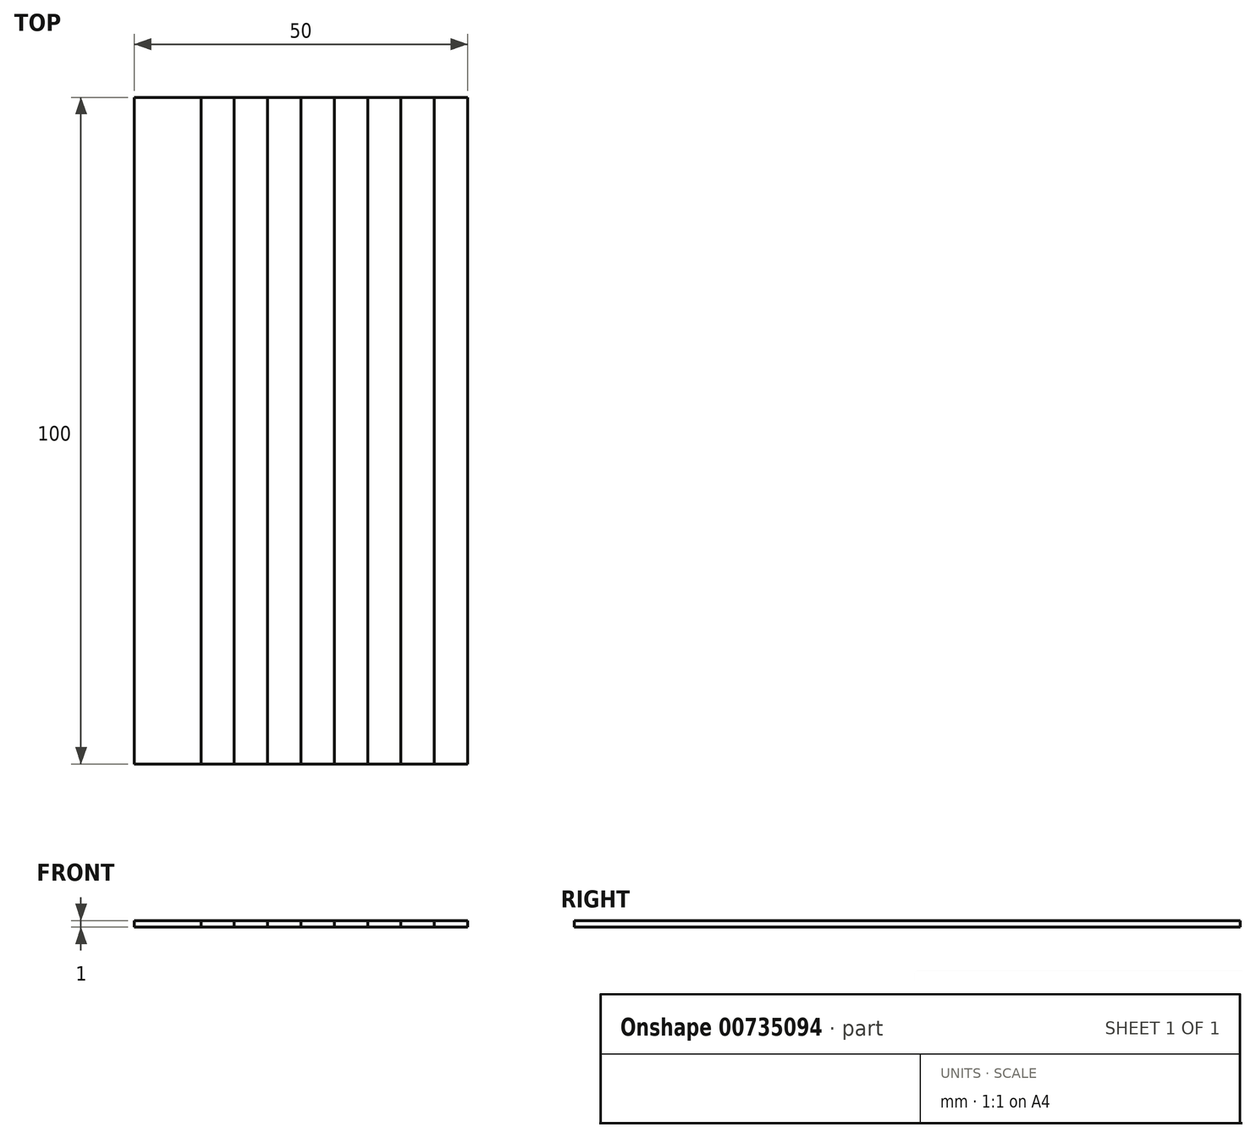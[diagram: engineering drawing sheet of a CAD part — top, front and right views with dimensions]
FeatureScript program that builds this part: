
annotation { "Feature Type Name" : "Feature", "Feature Type Description" : "" }
export const myFeature = defineFeature(function(context is Context, id is Id, definition is map)
    precondition{}
    {
        {
            var Q0;
            Q0=qCreatedBy(makeId("Top.planeOp"),FACE);
            var sketch = newSketch(context, id + "F0", { "sketchPlane" : qUnion([Q0])});
            skLineSegment(sketch, "E0.bottom", {"start": v(0, 50) * mm, "end": v(50, 50) * mm});
            skLineSegment(sketch, "E0.top", {"start": v(0, -50) * mm, "end": v(50, -50) * mm});
            skLineSegment(sketch, "E0.left", {"start": v(0, 50) * mm, "end": v(0, -50) * mm});
            skLineSegment(sketch, "E0.right", {"start": v(50, 50) * mm, "end": v(50, -50) * mm});
            skLineSegment(sketch, "E1", {"start": v(10, 50) * mm, "end": v(10, -50) * mm});
            skLineSegment(sketch, "E2", {"start": v(15, 50) * mm, "end": v(15, -50) * mm});
            skLineSegment(sketch, "E3", {"start": v(20, 50) * mm, "end": v(20, -50) * mm});
            skLineSegment(sketch, "E4", {"start": v(25, 50) * mm, "end": v(25, -50) * mm});
            skLineSegment(sketch, "E5", {"start": v(30, 50) * mm, "end": v(30, -50) * mm});
            skLineSegment(sketch, "E6", {"start": v(35, 50) * mm, "end": v(35, -50) * mm});
            skLineSegment(sketch, "E7", {"start": v(40, 50) * mm, "end": v(40, -50) * mm});
            skLineSegment(sketch, "E8", {"start": v(45, 50) * mm, "end": v(45, -50) * mm});
            skSolve(sketch);
        }
        {
            var Q0;
            {var subQ0=sQuery(id+"F0.wireOp",EDGE,"E0.left");Q0=makeQuery(id+"F0.imprint","IMPRINT",FACE,{"disambiguationData":[TD([[makeQuery(id+"F0.imprint","IMPRINT",EDGE,{"derivedFrom":subQ0}),1.0]])]});}
            var Q1;
            {var subQ0=sQuery(id+"F0.wireOp",EDGE,"E2");Q1=makeQuery(id+"F0.imprint","IMPRINT",FACE,{"disambiguationData":[TD([[makeQuery(id+"F0.imprint","IMPRINT",EDGE,{"derivedFrom":subQ0}),1.0]])]});}
            var Q2;
            {var subQ0=sQuery(id+"F0.wireOp",EDGE,"E4");Q2=makeQuery(id+"F0.imprint","IMPRINT",FACE,{"disambiguationData":[TD([[makeQuery(id+"F0.imprint","IMPRINT",EDGE,{"derivedFrom":subQ0}),1.0]])]});}
            var Q3;
            {var subQ0=sQuery(id+"F0.wireOp",EDGE,"E6");Q3=makeQuery(id+"F0.imprint","IMPRINT",FACE,{"disambiguationData":[TD([[makeQuery(id+"F0.imprint","IMPRINT",EDGE,{"derivedFrom":subQ0}),1.0]])]});}
            var Q4;
            {var subQ0=sQuery(id+"F0.wireOp",EDGE,"E0.right");Q4=makeQuery(id+"F0.imprint","IMPRINT",FACE,{"disambiguationData":[TD([[makeQuery(id+"F0.imprint","IMPRINT",EDGE,{"derivedFrom":subQ0}),-1.0]])]});}
            extrude(context, id + "F1", {"entities" : qUnion([Q0, Q1, Q2, Q3, Q4]), "endBound" : BoundingType.SYMMETRIC, "depth" : 1 * mm, "offsetDistance" : 25 * mm});
        }
        {
            var Q0;
            {var subQ0=sQuery(id+"F0.wireOp",EDGE,"E7");Q0=makeQuery(id+"F0.imprint","IMPRINT",FACE,{"disambiguationData":[TD([[makeQuery(id+"F0.imprint","IMPRINT",EDGE,{"derivedFrom":subQ0}),1.0]])]});}
            var Q1;
            {var subQ0=sQuery(id+"F0.wireOp",EDGE,"E5");Q1=makeQuery(id+"F0.imprint","IMPRINT",FACE,{"disambiguationData":[TD([[makeQuery(id+"F0.imprint","IMPRINT",EDGE,{"derivedFrom":subQ0}),1.0]])]});}
            var Q2;
            {var subQ0=sQuery(id+"F0.wireOp",EDGE,"E3");Q2=makeQuery(id+"F0.imprint","IMPRINT",FACE,{"disambiguationData":[TD([[makeQuery(id+"F0.imprint","IMPRINT",EDGE,{"derivedFrom":subQ0}),1.0]])]});}
            var Q3;
            {var subQ0=sQuery(id+"F0.wireOp",EDGE,"E1");Q3=makeQuery(id+"F0.imprint","IMPRINT",FACE,{"disambiguationData":[TD([[makeQuery(id+"F0.imprint","IMPRINT",EDGE,{"derivedFrom":subQ0}),1.0]])]});}
            extrude(context, id + "F2", {"entities" : qUnion([Q0, Q1, Q2, Q3]), "endBound" : BoundingType.SYMMETRIC, "depth" : 1 * mm, "offsetDistance" : 25 * mm});
        }
    });
